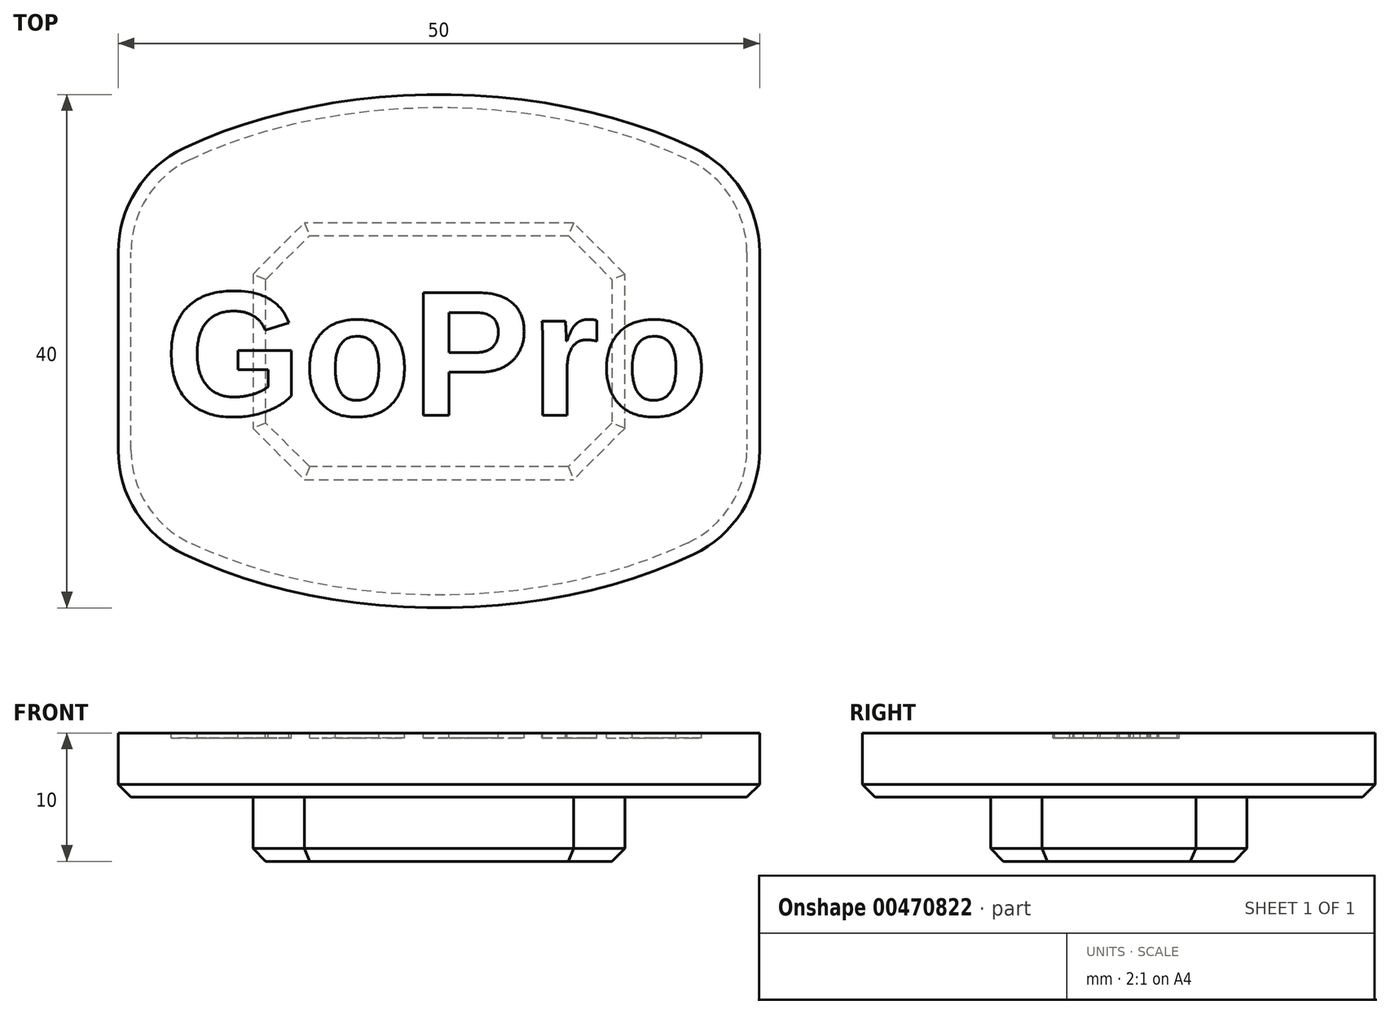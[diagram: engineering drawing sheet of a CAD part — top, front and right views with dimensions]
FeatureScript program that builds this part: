
annotation { "Feature Type Name" : "Feature", "Feature Type Description" : "" }
export const myFeature = defineFeature(function(context is Context, id is Id, definition is map)
    precondition{}
    {
        {
            var Q0;
            Q0=qCreatedBy(makeId("Top.planeOp"),FACE);
            var sketch = newSketch(context, id + "F0", { "sketchPlane" : qUnion([Q0])});
            skLineSegment(sketch, "E0.left", {"start": v(25, -7.7) * mm, "end": v(25, 7.7) * mm});
            skLineSegment(sketch, "E0.right", {"start": v(-25, -7.7) * mm, "end": v(-25, 7.7) * mm});
            skPoint(sketch, "E0.middle", {"position": v(0, 0) * mm});
            skEllipticalArc(sketch, "E1", {});
            skPoint(sketch, "E2.visualSharp", {"position": v(-25, 12.78) * mm});
            skArc(sketch, "E2.filletArc", {"start": v(-19.86, 15.83) * mm, "mid": v(-23.6, 12.5) * mm, "end": v(-25, 7.7) * mm});
            skArc(sketch, "E3.filletArc", {"start": v(-25, -7.7) * mm, "mid": v(-23.6, -12.5) * mm, "end": v(-19.86, -15.83) * mm});
            skEllipticalArc(sketch, "E4.trimOffspring", {});
            skPoint(sketch, "E5.visualSharp", {"position": v(25, 12.78) * mm});
            skArc(sketch, "E5.filletArc", {"start": v(25, 7.7) * mm, "mid": v(23.6, 12.5) * mm, "end": v(19.86, 15.83) * mm});
            skPoint(sketch, "E6.visualSharp", {"position": v(25, -12.78) * mm});
            skArc(sketch, "E6.filletArc", {"start": v(19.86, -15.83) * mm, "mid": v(23.6, -12.5) * mm, "end": v(25, -7.7) * mm});
            const initialGuessF0  = {"E1": [0, 0, 1, 0, 0.0325, 0.02, 4.054867696901255, 5.3699102638681255], "E4.trimOffspring": [0, 0, 1, 0, 0.0325, 0.02, 0.913275043311461, 2.2283176102783337]};
            skSetInitialGuess(sketch, initialGuessF0);
            skSolve(sketch);
        }
        {
            var Q0;
            Q0=makeQuery(id+"F0.imprint","IMPRINT",FACE,{"disambiguationData":[TD([[makeQuery(id+"F0.imprint","IMPRINT",EDGE,{"derivedFrom":sQuery(id+"F0.wireOp",EDGE,"E0.left")}),1.0]])]});
            extrude(context, id + "F1", {"entities" : qUnion([Q0]), "depth" : 5 * mm});
        }
        {
            var Q0;
            Q0=makeQuery(id+"F1.opExtrude","CAP_FACE",FACE,{"disambiguationData":[OSD([sQuery(id+"F0.wireOp",EDGE,"E0.left"),sQuery(id+"F0.wireOp",EDGE,"E0.right"),sQuery(id+"F0.wireOp",EDGE,"E1"),sQuery(id+"F0.wireOp",EDGE,"E2.filletArc"),sQuery(id+"F0.wireOp",EDGE,"E3.filletArc"),sQuery(id+"F0.wireOp",EDGE,"E4.trimOffspring"),sQuery(id+"F0.wireOp",EDGE,"E5.filletArc"),sQuery(id+"F0.wireOp",EDGE,"E6.filletArc")])],"isStart":true});
            var sketch = newSketch(context, id + "F2", { "sketchPlane" : qUnion([Q0])});
            skLineSegment(sketch, "E7.bottom", {"start": v(14.5, -10) * mm, "end": v(-14.5, -10) * mm});
            skLineSegment(sketch, "E7.top", {"start": v(14.5, 10) * mm, "end": v(-14.5, 10) * mm});
            skLineSegment(sketch, "E7.left", {"start": v(14.5, -10) * mm, "end": v(14.5, 10) * mm});
            skLineSegment(sketch, "E7.right", {"start": v(-14.5, -10) * mm, "end": v(-14.5, 10) * mm});
            skPoint(sketch, "E7.middle", {"position": v(0, 0) * mm});
            skSolve(sketch);
        }
        {
            var Q0;
            Q0=makeQuery(id+"F2.imprint","IMPRINT",FACE,{"disambiguationData":[TD([[makeQuery(id+"F2.imprint","IMPRINT",EDGE,{"derivedFrom":sQuery(id+"F2.wireOp",EDGE,"E7.bottom")}),-1.0]])]});
            extrude(context, id + "F3", {"entities" : qUnion([Q0]), "depth" : 5 * mm});
        }
        {
            var Q0;
            Q0=makeQuery(id+"F3.opExtrude","SWEPT_EDGE",EDGE,{"disambiguationData":[OSD([sQuery(id+"F2.wireOp",EDGE,"E7.top"),sQuery(id+"F2.wireOp",EDGE,"E7.right")])]});
            var Q1;
            Q1=makeQuery(id+"F3.opExtrude","SWEPT_EDGE",EDGE,{"disambiguationData":[OSD([sQuery(id+"F2.wireOp",EDGE,"E7.top"),sQuery(id+"F2.wireOp",EDGE,"E7.left")])]});
            var Q2;
            Q2=makeQuery(id+"F3.opExtrude","SWEPT_EDGE",EDGE,{"disambiguationData":[OSD([sQuery(id+"F2.wireOp",EDGE,"E7.bottom"),sQuery(id+"F2.wireOp",EDGE,"E7.left")])]});
            var Q3;
            Q3=makeQuery(id+"F3.opExtrude","SWEPT_EDGE",EDGE,{"disambiguationData":[OSD([sQuery(id+"F2.wireOp",EDGE,"E7.bottom"),sQuery(id+"F2.wireOp",EDGE,"E7.right")])]});
            chamfer(context, id + "F4", {"entities" : qUnion([Q0, Q1, Q2, Q3]), "width" : 4 * mm, "tangentPropagation" : true});
        }
        {
            var Q0;
            Q0=makeQuery(id+"F1.opExtrude","CAP_EDGE",EDGE,{"disambiguationData":[OSD([sQuery(id+"F0.wireOp",EDGE,"E1")])],"isStart":true});
            var Q1;
            Q1=makeQuery(id+"F3.opExtrude","CAP_FACE",FACE,{"disambiguationData":[OSD([sQuery(id+"F2.wireOp",EDGE,"E7.bottom"),sQuery(id+"F2.wireOp",EDGE,"E7.top"),sQuery(id+"F2.wireOp",EDGE,"E7.left"),sQuery(id+"F2.wireOp",EDGE,"E7.right")])],"isStart":false});
            chamfer(context, id + "F5", {"entities" : qUnion([Q0, Q1]), "width" : 1 * mm, "tangentPropagation" : true});
        }
        {
            var Q0;
            Q0=makeQuery(id+"F1.opExtrude","CAP_FACE",FACE,{"disambiguationData":[OSD([sQuery(id+"F0.wireOp",EDGE,"E0.left"),sQuery(id+"F0.wireOp",EDGE,"E0.right"),sQuery(id+"F0.wireOp",EDGE,"E1"),sQuery(id+"F0.wireOp",EDGE,"E2.filletArc"),sQuery(id+"F0.wireOp",EDGE,"E3.filletArc"),sQuery(id+"F0.wireOp",EDGE,"E4.trimOffspring"),sQuery(id+"F0.wireOp",EDGE,"E5.filletArc"),sQuery(id+"F0.wireOp",EDGE,"E6.filletArc")])],"isStart":false});
            var sketch = newSketch(context, id + "F6", { "sketchPlane" : qUnion([Q0])});
            skText(sketch, "E8", { "text": "GoPro", "fontName": "Arimo-Bold.ttf"});
            const initialGuessF6  = {"E8": [-0.02143, -0.005, 1, 0, 0.01]};
            skSetInitialGuess(sketch, initialGuessF6);
            skSolve(sketch);
        }
        {
            var Q0;
            Q0=makeQuery(id+"F6.imprint","IMPRINT",FACE,{"disambiguationData":[TD([[makeQuery(id+"F6.imprint","IMPRINT",EDGE,{"derivedFrom":sQuery(id+"F6.wireOp",EDGE,"E8.sketch_text.stroke-0")}),-1.0]])]});
            var Q1;
            Q1=makeQuery(id+"F6.imprint","IMPRINT",FACE,{"disambiguationData":[TD([[makeQuery(id+"F6.imprint","IMPRINT",EDGE,{"derivedFrom":sQuery(id+"F6.wireOp",EDGE,"E8.sketch_text.stroke-21")}),-1.0]])]});
            var Q2;
            Q2=makeQuery(id+"F6.imprint","IMPRINT",FACE,{"disambiguationData":[TD([[makeQuery(id+"F6.imprint","IMPRINT",EDGE,{"derivedFrom":sQuery(id+"F6.wireOp",EDGE,"E8.sketch_text.stroke-35")}),-1.0]])]});
            var Q3;
            Q3=makeQuery(id+"F6.imprint","IMPRINT",FACE,{"disambiguationData":[TD([[makeQuery(id+"F6.imprint","IMPRINT",EDGE,{"derivedFrom":sQuery(id+"F6.wireOp",EDGE,"E8.sketch_text.stroke-51")}),-1.0]])]});
            var Q4;
            Q4=makeQuery(id+"F6.imprint","IMPRINT",FACE,{"disambiguationData":[TD([[makeQuery(id+"F6.imprint","IMPRINT",EDGE,{"derivedFrom":sQuery(id+"F6.wireOp",EDGE,"E8.sketch_text.stroke-68")}),-1.0]])]});
            extrude(context, id + "F7", {"entities" : qUnion([Q0, Q1, Q2, Q3, Q4]), "operationType" : NewBodyOperationType.REMOVE, "oppositeDirection" : true, "depth" : .4 * mm});
        }
    });
